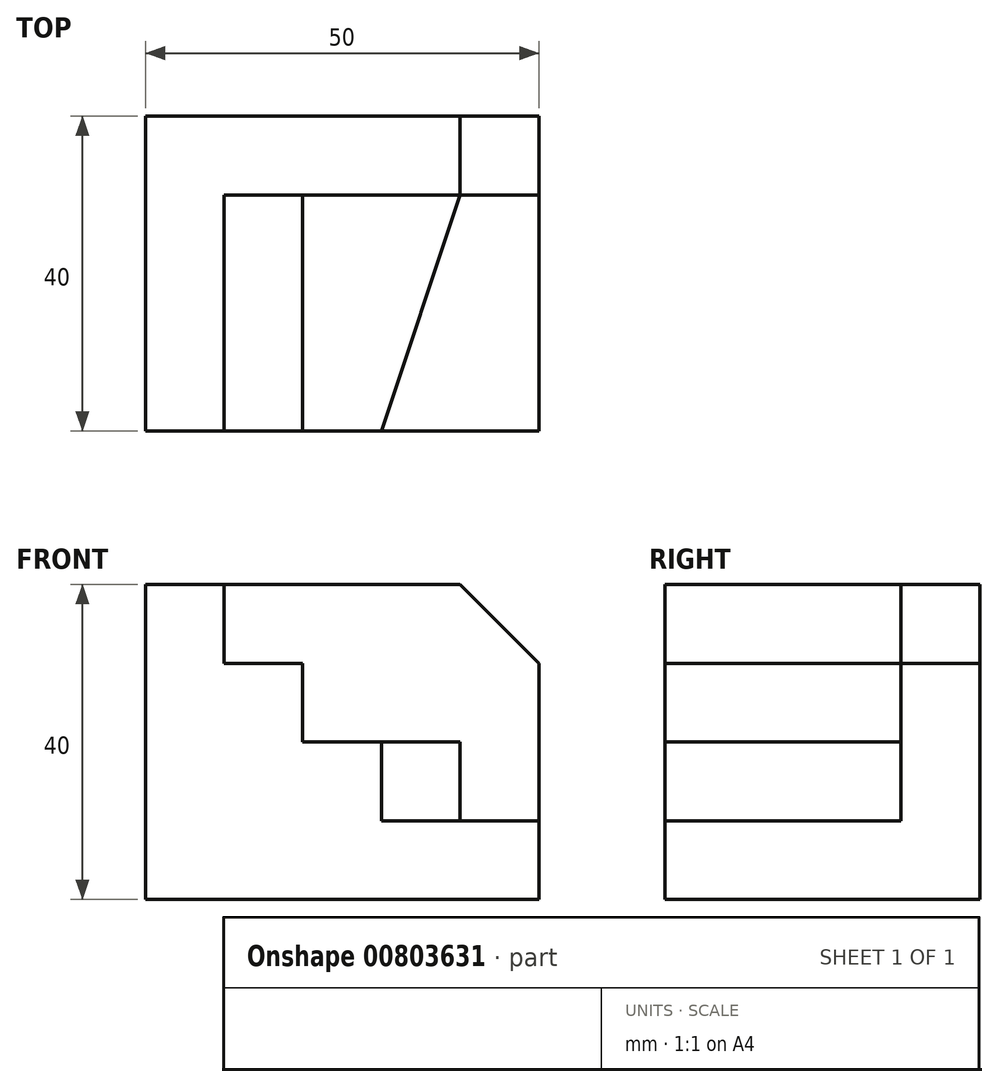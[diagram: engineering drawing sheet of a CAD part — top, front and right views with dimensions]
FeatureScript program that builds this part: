
annotation { "Feature Type Name" : "Feature", "Feature Type Description" : "" }
export const myFeature = defineFeature(function(context is Context, id is Id, definition is map)
    precondition{}
    {
        {
            var Q0;
            Q0=qCreatedBy(makeId("Top.planeOp"),FACE);
            var sketch = newSketch(context, id + "F0", { "sketchPlane" : qUnion([Q0])});
            skLineSegment(sketch, "E0.bottom", {"start": v(0, 0) * mm, "end": v(50, 0) * mm});
            skLineSegment(sketch, "E0.top", {"start": v(0, 40) * mm, "end": v(50, 40) * mm});
            skLineSegment(sketch, "E0.left", {"start": v(0, 0) * mm, "end": v(0, 40) * mm});
            skLineSegment(sketch, "E0.right", {"start": v(50, 0) * mm, "end": v(50, 40) * mm});
            skLineSegment(sketch, "E1", {"start": v(10, 0) * mm, "end": v(10, 30) * mm});
            skLineSegment(sketch, "E2", {"start": v(10, 30) * mm, "end": v(50, 30) * mm});
            skLineSegment(sketch, "E3", {"start": v(20, 30) * mm, "end": v(20, 0) * mm});
            skLineSegment(sketch, "E4", {"start": v(30, 0) * mm, "end": v(40, 30) * mm});
            skSolve(sketch);
        }
        {
            var Q0;
            {var subQ1=sQuery(id+"F0.wireOp",EDGE,"E0.top");Q0=makeQuery(id+"F0.imprint","IMPRINT",FACE,{"disambiguationData":[TD([[makeQuery(id+"F0.imprint","IMPRINT",EDGE,{"derivedFrom":subQ1}),-1.0]])]});}
            extrude(context, id + "F1", {"entities" : qUnion([Q0]), "depth" : 40 * mm, "offsetDistance" : 25 * mm});
        }
        {
            var Q0;
            {var subQ0=sQuery(id+"F0.wireOp",EDGE,"E1");Q0=makeQuery(id+"F0.imprint","IMPRINT",FACE,{"disambiguationData":[TD([[makeQuery(id+"F0.imprint","IMPRINT",EDGE,{"derivedFrom":subQ0}),-1.0]])]});}
            extrude(context, id + "F2", {"entities" : qUnion([Q0]), "operationType" : NewBodyOperationType.ADD, "depth" : 30 * mm, "offsetDistance" : 25 * mm});
        }
        {
            var Q0;
            {var subQ0=sQuery(id+"F0.wireOp",EDGE,"E3");Q0=makeQuery(id+"F0.imprint","IMPRINT",FACE,{"disambiguationData":[TD([[makeQuery(id+"F0.imprint","IMPRINT",EDGE,{"derivedFrom":subQ0}),1.0]])]});}
            extrude(context, id + "F3", {"entities" : qUnion([Q0]), "operationType" : NewBodyOperationType.ADD, "depth" : 20 * mm, "offsetDistance" : 25 * mm});
        }
        {
            var Q0;
            {var subQ3=sQuery(id+"F0.wireOp",EDGE,"E4");Q0=makeQuery(id+"F0.imprint","IMPRINT",FACE,{"disambiguationData":[TD([[makeQuery(id+"F0.imprint","IMPRINT",EDGE,{"derivedFrom":subQ3}),-1.0]])]});}
            extrude(context, id + "F4", {"entities" : qUnion([Q0]), "operationType" : NewBodyOperationType.ADD, "depth" : 10 * mm, "offsetDistance" : 25 * mm});
        }
        {
            var Q0;
            Q0=makeQuery(id+"F1.opExtrude","CAP_EDGE",EDGE,{"disambiguationData":[OSD([sQuery(id+"F0.wireOp",EDGE,"E0.right")])],"isStart":false});
            chamfer(context, id + "F5", {"entities" : qUnion([Q0]), "width" : 10 * mm, "tangentPropagation" : true});
        }
    });
